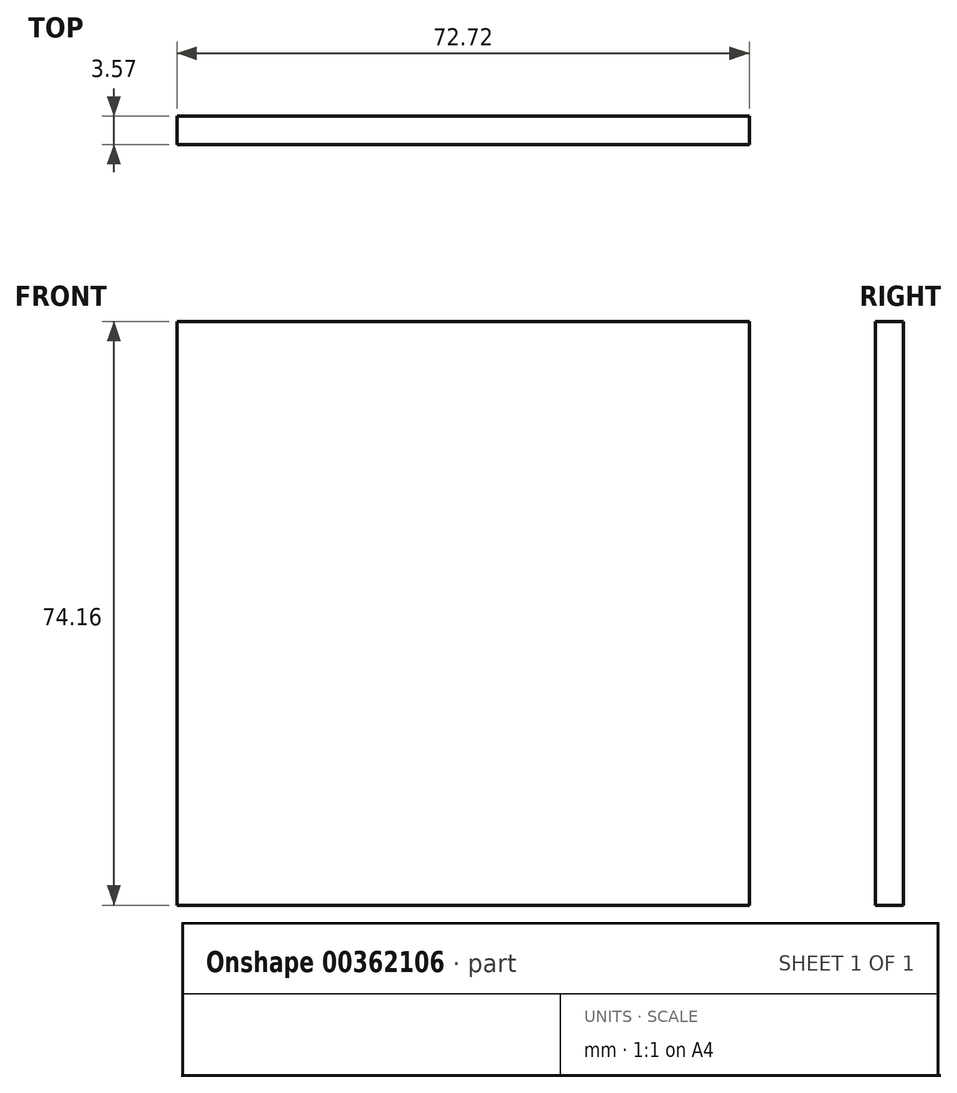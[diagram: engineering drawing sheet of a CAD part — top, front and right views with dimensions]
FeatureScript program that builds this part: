
annotation { "Feature Type Name" : "Feature", "Feature Type Description" : "" }
export const myFeature = defineFeature(function(context is Context, id is Id, definition is map)
    precondition{}
    {
        {
            var Q0;
            Q0=qCreatedBy(makeId("Front.planeOp"),FACE);
            var sketch = newSketch(context, id + "F0", { "sketchPlane" : qUnion([Q0])});
            skLineSegment(sketch, "E0.bottom", {"start": v(42.22, 37.08) * mm, "end": v(-30.5, 37.08) * mm});
            skLineSegment(sketch, "E0.top", {"start": v(42.22, -37.08) * mm, "end": v(-30.5, -37.08) * mm});
            skLineSegment(sketch, "E0.left", {"start": v(42.22, 37.08) * mm, "end": v(42.22, -37.08) * mm});
            skLineSegment(sketch, "E0.right", {"start": v(-30.5, 37.08) * mm, "end": v(-30.5, -37.08) * mm});
            skPoint(sketch, "E0.middle", {"position": v(5.86, 0) * mm});
            skSolve(sketch);
        }
        {
            var Q0;
            Q0=makeQuery(id+"F0.imprint","IMPRINT",FACE,{"disambiguationData":[TD([[makeQuery(id+"F0.imprint","IMPRINT",EDGE,{"derivedFrom":sQuery(id+"F0.wireOp",EDGE,"E0.bottom")}),1.0]])]});
            extrude(context, id + "F1", {"entities" : qUnion([Q0]), "depth" : 3.57 * mm});
        }
    });
